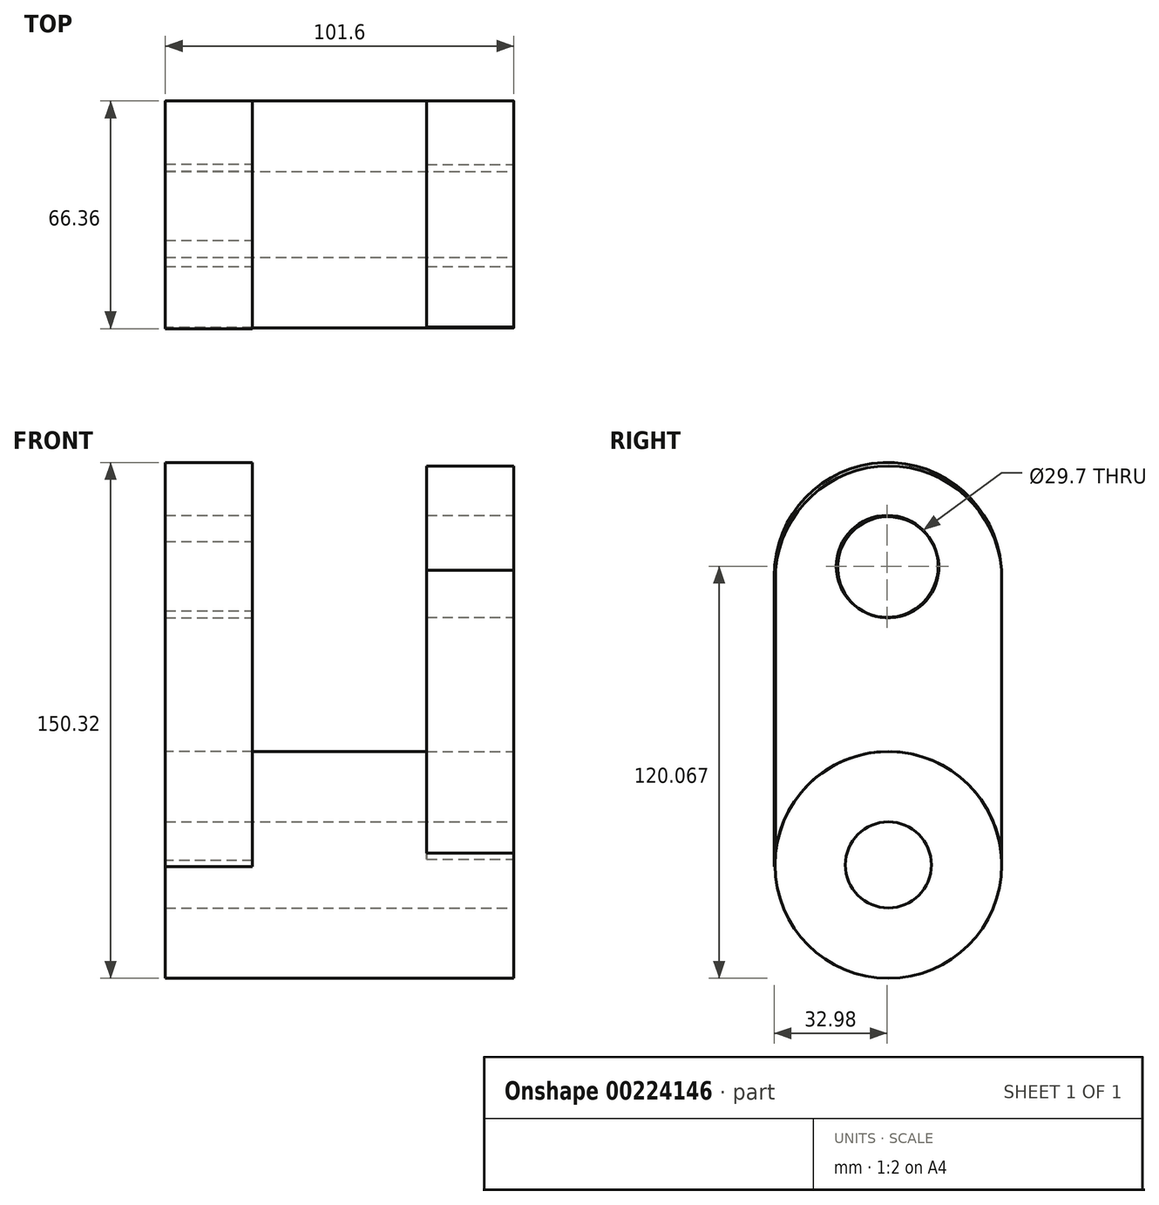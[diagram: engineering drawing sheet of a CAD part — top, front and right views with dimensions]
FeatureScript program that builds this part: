
annotation { "Feature Type Name" : "Feature", "Feature Type Description" : "" }
export const myFeature = defineFeature(function(context is Context, id is Id, definition is map)
    precondition{}
    {
        {
            var Q0;
            Q0=qCreatedBy(makeId("Right.planeOp"),FACE);
            var sketch = newSketch(context, id + "F0", { "sketchPlane" : qUnion([Q0])});
            skCircle(sketch, "E0", {"center": v(36.1, -52.73) * mm, "radius": 33.04 * mm});
            skSolve(sketch);
        }
        {
            var Q0;
            Q0 = qSketchRegion(id + "F0", true);
            extrude(context, id + "F1", {"entities" : qUnion([Q0]), "depth" : 101.6 * mm});
        }
        {
            var Q0;
            Q0=makeQuery(id+"F1.opExtrude","CAP_FACE",FACE,{"disambiguationData":[OSD([sQuery(id+"F0.wireOp",EDGE,"E0")])],"isStart":true});
            var sketch = newSketch(context, id + "F2", { "sketchPlane" : qUnion([Q0])});
            skLineSegment(sketch, "E1.bottom", {"start": v(-69.13, 31.37) * mm, "end": v(-2.79, 31.37) * mm});
            skLineSegment(sketch, "E1.top", {"start": v(-69.13, -53.19) * mm, "end": v(-2.79, -53.19) * mm});
            skLineSegment(sketch, "E1.left", {"start": v(-69.13, 31.37) * mm, "end": v(-69.13, -53.19) * mm});
            skLineSegment(sketch, "E1.right", {"start": v(-2.79, 31.37) * mm, "end": v(-2.79, -53.19) * mm});
            skPoint(sketch, "E1.middle", {"position": v(-35.96, -10.9) * mm});
            skArc(sketch, "E2", {"start": v(-2.79, 31.37) * mm, "mid": v(-35.96, 64.54) * mm, "end": v(-69.13, 31.37) * mm});
            skSolve(sketch);
        }
        {
            var Q0;
            {var subQ2=sQuery(id+"F2.wireOp",EDGE,"E1.bottom");Q0=makeQuery(id+"F2.imprint","IMPRINT",FACE,{"disambiguationData":[TD([[makeQuery(id+"F2.imprint","IMPRINT",EDGE,{"derivedFrom":subQ2}),-1.0]])]});}
            var Q1;
            Q1=makeQuery(id+"F2.imprint","IMPRINT",FACE,{"disambiguationData":[TD([[makeQuery(id+"F2.imprint","IMPRINT",EDGE,{"derivedFrom":sQuery(id+"F2.wireOp",EDGE,"E1.bottom")}),1.0]])]});
            extrude(context, id + "F3", {"entities" : qUnion([Q0, Q1]), "oppositeDirection" : true, "depth" : 25.4 * mm});
        }
        {
            var Q0;
            Q0=makeQuery(id+"F1.opExtrude","CAP_FACE",FACE,{"disambiguationData":[OSD([sQuery(id+"F0.wireOp",EDGE,"E0")])],"isStart":false});
            var sketch = newSketch(context, id + "F4", { "sketchPlane" : qUnion([Q0])});
            skLineSegment(sketch, "E3.bottom", {"start": v(3.25, 33.1) * mm, "end": v(69.1, 33.1) * mm});
            skLineSegment(sketch, "E3.top", {"start": v(3.25, -51.04) * mm, "end": v(69.1, -51.04) * mm});
            skLineSegment(sketch, "E3.left", {"start": v(3.25, 33.1) * mm, "end": v(3.25, -51.04) * mm});
            skLineSegment(sketch, "E3.right", {"start": v(69.1, 33.1) * mm, "end": v(69.1, -51.04) * mm});
            skArc(sketch, "E4", {"start": v(69.1, 33.1) * mm, "mid": v(36.18, 63.54) * mm, "end": v(3.25, 33.1) * mm});
            skSolve(sketch);
        }
        {
            var Q0;
            Q0=makeQuery(id+"F4.imprint","IMPRINT",FACE,{"disambiguationData":[TD([[makeQuery(id+"F4.imprint","IMPRINT",EDGE,{"derivedFrom":sQuery(id+"F4.wireOp",EDGE,"E3.bottom")}),1.0]])]});
            var Q1;
            {var subQ0=sQuery(id+"F4.wireOp",EDGE,"E3.bottom");Q1=makeQuery(id+"F4.imprint","IMPRINT",FACE,{"disambiguationData":[TD([[makeQuery(id+"F4.imprint","IMPRINT",EDGE,{"derivedFrom":subQ0}),-1.0]])]});}
            extrude(context, id + "F5", {"entities" : qUnion([Q0, Q1]), "oppositeDirection" : true, "depth" : 25.4 * mm});
        }
        {
            var Q0;
            Q0=makeQuery(id+"F1.opExtrude","CAP_FACE",FACE,{"disambiguationData":[OSD([sQuery(id+"F0.wireOp",EDGE,"E0")])],"isStart":false});
            var sketch = newSketch(context, id + "F6", { "sketchPlane" : qUnion([Q0])});
            skCircle(sketch, "E5", {"center": v(36.1, -52.73) * mm, "radius": 12.53 * mm});
            skSolve(sketch);
        }
        {
            var Q0;
            Q0 = qSketchRegion(id + "F6", true);
            extrude(context, id + "F7", {"entities" : qUnion([Q0]), "operationType" : NewBodyOperationType.REMOVE, "endBound" : BoundingType.THROUGH_ALL, "oppositeDirection" : true, "depth" : 25.4 * mm});
        }
        {
            var Q0;
            Q0=makeQuery(id+"F5.opExtrude","CAP_FACE",FACE,{"disambiguationData":[OSD([sQuery(id+"F0.wireOp",EDGE,"E0"),sQuery(id+"F4.wireOp",EDGE,"E3.left"),sQuery(id+"F4.wireOp",EDGE,"E3.right"),sQuery(id+"F4.wireOp",EDGE,"E4")])],"isStart":true});
            var sketch = newSketch(context, id + "F8", { "sketchPlane" : qUnion([Q0])});
            skCircle(sketch, "E6", {"center": v(35.77, 34.29) * mm, "radius": 14.85 * mm});
            skSolve(sketch);
        }
        {
            var Q0;
            Q0 = qSketchRegion(id + "F8", true);
            extrude(context, id + "F9", {"entities" : qUnion([Q0]), "operationType" : NewBodyOperationType.REMOVE, "oppositeDirection" : true, "depth" : 116.84 * mm});
        }
        {
            var Q0;
            Q0=makeQuery(id+"F3.opExtrude","CAP_FACE",FACE,{"disambiguationData":[OSD([sQuery(id+"F0.wireOp",EDGE,"E0"),sQuery(id+"F2.wireOp",EDGE,"E1.top"),sQuery(id+"F2.wireOp",EDGE,"E1.left"),sQuery(id+"F2.wireOp",EDGE,"E1.right"),sQuery(id+"F2.wireOp",EDGE,"E2")])],"isStart":false});
            var sketch = newSketch(context, id + "F10", { "sketchPlane" : qUnion([Q0])});
            skCircle(sketch, "E7", {"center": v(36.07, 33.99) * mm, "radius": 14.74 * mm});
            skSolve(sketch);
        }
        {
            var Q0;
            Q0 = qSketchRegion(id + "F10", true);
            extrude(context, id + "F11", {"entities" : qUnion([Q0]), "operationType" : NewBodyOperationType.REMOVE, "endBound" : BoundingType.THROUGH_ALL, "oppositeDirection" : true, "depth" : 25.4 * mm});
        }
    });
